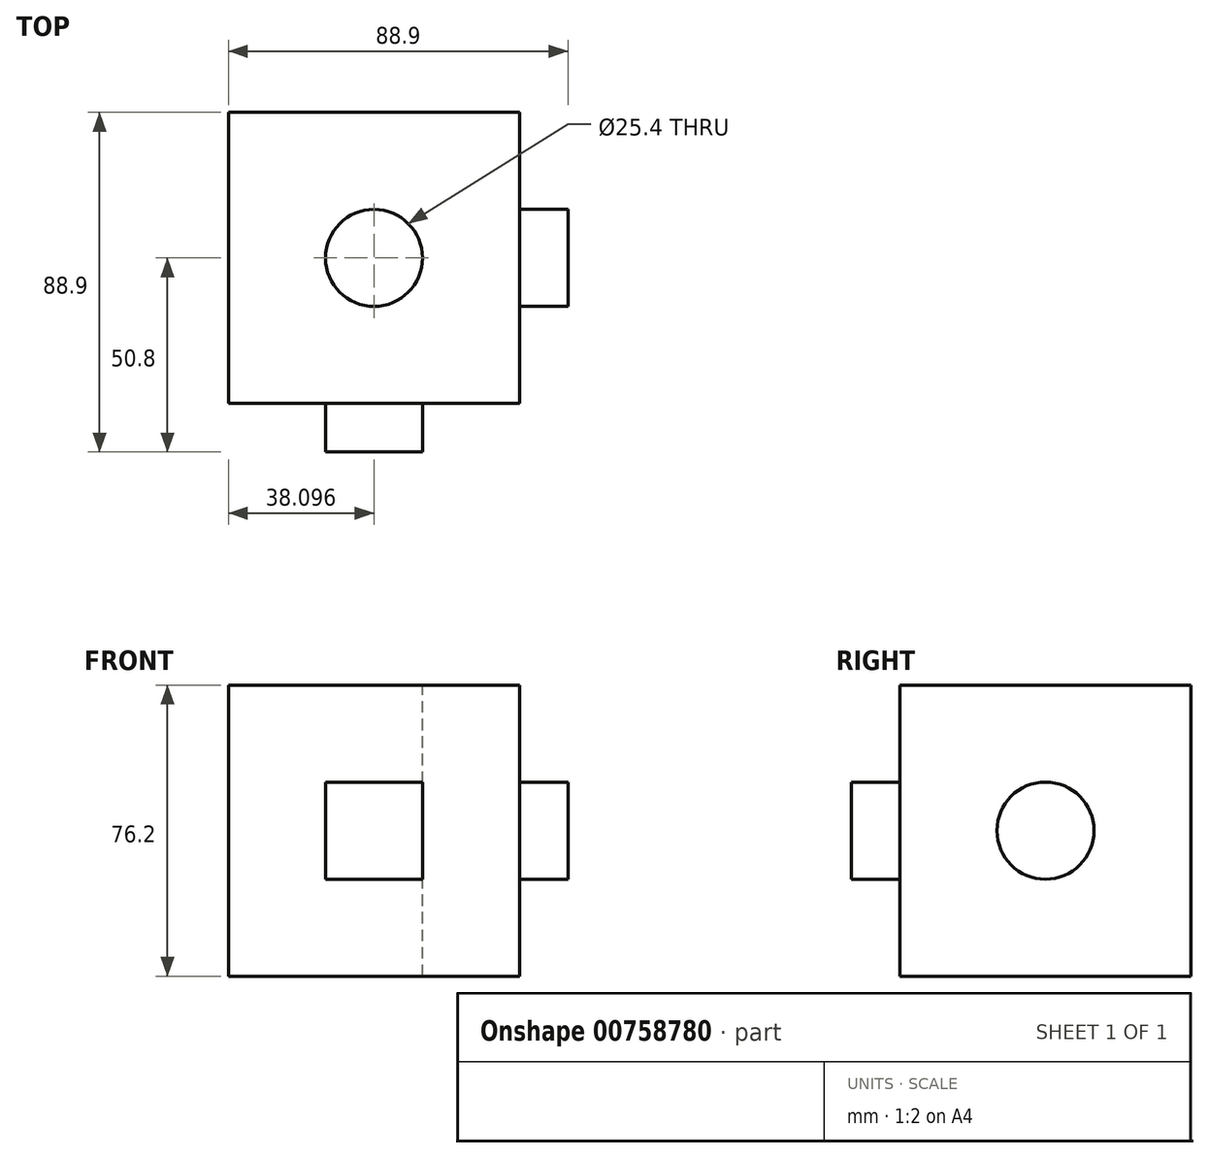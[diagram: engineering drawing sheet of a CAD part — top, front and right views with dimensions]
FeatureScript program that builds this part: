
annotation { "Feature Type Name" : "Feature", "Feature Type Description" : "" }
export const myFeature = defineFeature(function(context is Context, id is Id, definition is map)
    precondition{}
    {
        {
            var Q0;
            Q0=qCreatedBy(makeId("Front.planeOp"),FACE);
            var sketch = newSketch(context, id + "F0", { "sketchPlane" : qUnion([Q0])});
            skLineSegment(sketch, "E0.bottom", {"start": v(-49.03, 73.92) * mm, "end": v(-125.23, 73.92) * mm});
            skLineSegment(sketch, "E0.top", {"start": v(-49.03, -2.28) * mm, "end": v(-125.23, -2.28) * mm});
            skLineSegment(sketch, "E0.left", {"start": v(-49.03, 73.92) * mm, "end": v(-49.03, -2.28) * mm});
            skLineSegment(sketch, "E0.right", {"start": v(-125.23, 73.92) * mm, "end": v(-125.23, -2.28) * mm});
            skSolve(sketch);
        }
        {
            var Q0;
            Q0=makeQuery(id+"F0.imprint","IMPRINT",FACE,{"disambiguationData":[TD([[makeQuery(id+"F0.imprint","IMPRINT",EDGE,{"derivedFrom":sQuery(id+"F0.wireOp",EDGE,"E0.bottom")}),1.0]])]});
            extrude(context, id + "F1", {"entities" : qUnion([Q0]), "depth" : 76.2 * mm, "offsetDistance" : 25.4 * mm});
        }
        {
            var Q0;
            Q0=makeQuery(id+"F1.opExtrude","CAP_FACE",FACE,{"disambiguationData":[OSD([sQuery(id+"F0.wireOp",EDGE,"E0.bottom"),sQuery(id+"F0.wireOp",EDGE,"E0.top"),sQuery(id+"F0.wireOp",EDGE,"E0.left"),sQuery(id+"F0.wireOp",EDGE,"E0.right")])],"isStart":false});
            var sketch = newSketch(context, id + "F2", { "sketchPlane" : qUnion([Q0])});
            skPoint(sketch, "E1.firstSnap0", {"position": v(-125.23, 48.52) * mm});
            skLineSegment(sketch, "E1.bottom", {"start": v(-99.83, 48.52) * mm, "end": v(-74.43, 48.52) * mm});
            skLineSegment(sketch, "E1.top", {"start": v(-99.83, 23.12) * mm, "end": v(-74.43, 23.12) * mm});
            skLineSegment(sketch, "E1.left", {"start": v(-99.83, 48.52) * mm, "end": v(-99.83, 23.12) * mm});
            skLineSegment(sketch, "E1.right", {"start": v(-74.43, 48.52) * mm, "end": v(-74.43, 23.12) * mm});
            skSolve(sketch);
        }
        {
            var Q0;
            Q0=makeQuery(id+"F2.imprint","IMPRINT",FACE,{"disambiguationData":[TD([[makeQuery(id+"F2.imprint","IMPRINT",EDGE,{"derivedFrom":sQuery(id+"F2.wireOp",EDGE,"E1.bottom")}),-1.0]])]});
            extrude(context, id + "F3", {"entities" : qUnion([Q0]), "operationType" : NewBodyOperationType.ADD, "depth" : 12.7 * mm, "offsetDistance" : 25.4 * mm});
        }
        {
            var Q0;
            Q0=makeQuery(id+"F1.opExtrude","SWEPT_FACE",FACE,{"disambiguationData":[OSD([sQuery(id+"F0.wireOp",EDGE,"E0.left")])]});
            var sketch = newSketch(context, id + "F4", { "sketchPlane" : qUnion([Q0])});
            skSolve(sketch);
        }
        {
            var Q0;
            {var subQ0=sQuery(id+"F0.wireOp",EDGE,"E0.left");Q0=makeQuery(id+"F4.imprint","IMPRINT",FACE,{"disambiguationData":[TD([[makeQuery(id+"F4.imprint","IMPRINT",EDGE,{"derivedFrom":makeQuery(id+"F1.opExtrude","CAP_EDGE",EDGE,{"disambiguationData":[OSD([subQ0])],"isStart":true})}),-1.0]])]});}
            var sketch = newSketch(context, id + "F5", { "sketchPlane" : qUnion([Q0])});
            skCircle(sketch, "E2", {"center": v(-38.1, 35.82) * mm, "radius": 12.7 * mm});
            skSolve(sketch);
        }
        {
            var Q0;
            Q0=makeQuery(id+"F5.imprint","IMPRINT",FACE,{"disambiguationData":[TD([[makeQuery(id+"F5.imprint","IMPRINT",EDGE,{"derivedFrom":sQuery(id+"F5.wireOp",EDGE,"E2")}),1.0]])]});
            extrude(context, id + "F6", {"entities" : qUnion([Q0]), "operationType" : NewBodyOperationType.ADD, "depth" : 12.7 * mm, "offsetDistance" : 25.4 * mm});
        }
        {
            var Q0;
            Q0=makeQuery(id+"F1.opExtrude","SWEPT_FACE",FACE,{"disambiguationData":[OSD([sQuery(id+"F0.wireOp",EDGE,"E0.bottom")])]});
            var sketch = newSketch(context, id + "F7", { "sketchPlane" : qUnion([Q0])});
            skPoint(sketch, "E3", {"position": v(-87.13, -38.1) * mm});
            skSolve(sketch);
        }
        {
            var Q0;
            Q0=sQuery(id+"F7.wireOp",VERTEX,"E3");
            var Q1;
            Q1=makeQuery(id+"F1.opExtrude","SWEPT_BODY",BODY,{"disambiguationData":[OSD([sQuery(id+"F0.wireOp",EDGE,"E0.bottom"),sQuery(id+"F0.wireOp",EDGE,"E0.top"),sQuery(id+"F0.wireOp",EDGE,"E0.left"),sQuery(id+"F0.wireOp",EDGE,"E0.right")])]});
            hole(context, id + "F8", {"style" : HoleStyle.SIMPLE, "endStyle" : HoleEndStyle.THROUGH, "holeDiameter" : 25.4 * mm, "majorDiameter" : 6.35 * mm, "isTappedThrough" : true, "tappedDepth" : 12.7 * mm, "tapClearance" : 3, "locations" : qUnion([Q0]), "scope" : qUnion([Q1])});
        }
    });
